# Revit family: Gira_216300
name_source: partatom
category: Elektroinstallationen
revit_build: Autodesk Revit 2017 (Build: 20160225_1515(x64)
units: mm (PartAtom-declared; Revit-internal decimal feet)

## family parameters
Basisbauteil = Fläche
Beim Laden mit Abzugskörper schneiden = Nein
Bemaßung runder Anschluss = Durchmesser verwenden
Beschriftungsausrichtung beibehalten = Nein
Gemeinsam genutzt = Nein
Raumberechnungspunkt = Nein
Teiletyp = Normal

## types (1)
- Fan Coil Aktor KNX REG
    Andere Bussysteme = ohne
    Anzahl der Ausgänge = 0
    Anzahl der binären Eingänge = 0
    BIM = https://media.stage.bim.site 8f.rfa
    BIMSITE_PRODUCT_ID = e50a8b9e110624fc39c6d2d0b3aa76b6184317be
    Beschreibung = KNX Fan Coil Aktor  REG plus Merkmale:  Fan Coil Aktor zur Ansteuerung von Gebläsekonvektoren (Fan Coil Units), die zur Klimatisierung von Räumen eingesetzt werden.  Der Aktor empfängt Telegramme, z. B. von einem Raumtemperaturregler, und setzt die Stellgrößentelegramme in dazu äquivalente Lüfterstufen und Ventilstellungen um.  Anschluss eines Gebläsekonvektors mit bis zu sechs Lüfterstufen oder Anschluss von zwei Gebläsekonvektoren mit jeweils bis zu zwei Lüfterstufen bei 2-Rohr-Systemen.  Handbetätigung.  Baustellenbetrieb: Ausgänge manuell bedienbar ohne Busspannung nur mit der Betriebsspannung.  Betriebsarten für Heiz- oder Kühlbetrieb, oder kombinierten Heiz- und Kühlbetrieb.  2-Rohr- oder 4-Rohrbetrieb. 2-Rohrsystem heizt oder kühlt über eine gemeinsamen Wasserkreislauf. 4-Rohrsystem besteht aus getrennten Vor- und Rücklauf für das Heiz- und Kühlsystem.  Einzelnes oder hierarchisches Schalten der Lüfterstufen.  Rückmeldung, Ausgangsanzeige, Sperrfunktion für jeden Kanal, Stufenbegrenzung.  Verhalten bei Busspannungsausfall oder Bus- Netzspannungsausfall und nach einem ETS-Programmiervorgang konfigurierbar.  Grenzwerte einstellbar.  Zyklisches oder ereignisorientiertes Senden.  Freie Kanäle können für Schaltfunktionen, z. B. Raumbeleuchtung, genutzt werden.  Hinweise :  VDE-Zulassung gemäß EN 60669-1, EN 60669-2-1.  Montage auf DIN-Hutschiene.
    Blindleistung = Nein
    Breite in Teilungseinheiten = 4
    Busspannung pufferbar = Nein
    Bussystem Funkbus = Nein
    Bussystem KNX = Ja
    Bussystem KNX-Funk = Nein
    Bussystem LON = Nein
    Bussystem Powernet = Nein
    Datenblatt = https://media.stage.bim.site
    Datenblatt 1 = https://media.stage.bim.site
    GTIN = 4010337059387
    Geeignet für C-Last = Nein
    HAN = 216300
    HeinzeBIM = https://www.heinze.de
    Hersteller = Gira
    Kosten = 0 $
    Max. Anzahl der Schaltausgänge = 2
    Mit Busankopplung = Nein
    Mit LED-Anzeige = Nein
    Modulare Erweiterungsmöglichkeit = Nein
    Montageart = REG
    Produktseite = https://media.stage.bim.site
    Tarifumschaltung = Nein
    Typname = Fan Coil Aktor KNX REG
    URL = https://www.gira.de
    Verschiedene Phasen anschließbar = Nein
    Vor Ort-/Handbedienung = Nein
    Vorgabe-Ansicht = 1219 mm
    Zulassung nach PTB = Nein

## geometry (parser evidence)
native form markers: Sweep x3
no freeform markers — native parametric forms only
